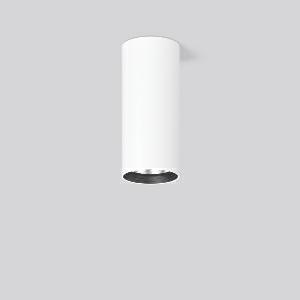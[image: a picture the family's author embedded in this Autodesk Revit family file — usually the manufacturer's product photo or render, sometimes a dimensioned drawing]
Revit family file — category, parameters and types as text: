
# Revit family: heledon_mini_a_931202_002_2_76_d9cf
name_source: partatom
category: Lighting Fixtures
units: mm (PartAtom-declared; Revit-internal decimal feet)

## family parameters
Cut with Voids When Loaded = No
Host = Face
Light Source = No
Part Type = Normal
Room Calculation Point = No
Round Connector Dimension = Use Diameter
Shared = No

## types (1)
- HELEDON mini A (1 x LED Modul 927, 2400 lm, 2700)
    Apparent Load = 20 VA
    Approval mark = CE
    CIE Flux Codes = 95 99 100 100 100
    Color Rendering = 92
    Color Temperature = 2700
    Default Elevation = 1800 mm
    Description = Series: HELEDON mini
Cylindrical surface-mounted downlight. Housing: die-cast aluminium, powder-coated. Internal ceiling frame polycarbonate with bayonet mounting. Black plastic ring and recessed LED to prevent glare from the side. Optical assembly with reflector made of MIRO-Silver with 98% total light reflection for outstanding efficiency - can be changed without tools. Best colour rendering index Ra>90. Suitable for Ceiling mounting. Easy installation with a separate ceiling frame with bayonet mounting and plug connection. Driver integrated. Connected via plug-in connector. High quality converter without flickering and stroboscopic effect. The following accessories can be mounted without use of tools: interchangeable lenses, decorative glasses, honeycomb louvre, clear and frosted diffusers, white interchangeable plastic ring. 
Colour: traffic white, matt (RAL 9016)
Diameter: 87 mm
Height: 197 mm
Lamp: LED
Socket: without socket
Colour temperature: 2700K
Colour rendering index (CRI): 92
System power: 20 W
Rated luminous flux: 2400 lm
Luminous efficiency: 120 lm/W
Control gear: Converter, dimmable, DALI
Protection class: I
Type of protection: IP 20
    Height = 197 mm
    Lamp = 1 x LED Modul 927
    Lamp Light Flux = 2400 lm
    Lamp count = 1
    Length = 87 mm
    Lifetime = 50000 h
    Luminous efficacy = 120 lm/W
    Manufacturer = RZB
    ModVariant = No
    Model = 931202.002.2.76
    Mounting Place = Ceiling
    Mounting Type = Surface mounted
    Number of Poles = 1
    OnlyDefault = Yes
    Power Factor = 1
    Product Name = HELEDON mini A
    Product group = Surface mounted downlights
    ProductGroupID = 302
    Protection Class = Protection class I
    Protection Degree = IP 20
    RLX_Detail_Level = 1
    RLX_Emergency_Light_Flux = 0 lm
    RLX_Emergency_Type = 0
    RLX_Emergency_Type_DB = No
    RlxData = <blob elided: 105809 chars, md5=02c031b2>
    Socket = socket
    Standby Power = 0 W
    System Light Flux = 2400 lm
    System Power = 20 W
    Type Comments = Product without accessories
    Type Image = 931188.002.jpg
    URL = http://relux.com
    VarID = ---
    Voltage = 230 V
    Voltage Range = 220-240 V
    Weight = 0.00 kg
    Width = 0 mm  [stored 0 ft]

note: [stored X ft] marks values corroborated as IEEE doubles in the binary element streams (Revit-internal decimal feet)

## geometry (parser evidence)
native form markers: Blend x4, Sweep x9
no freeform markers — native parametric forms only
